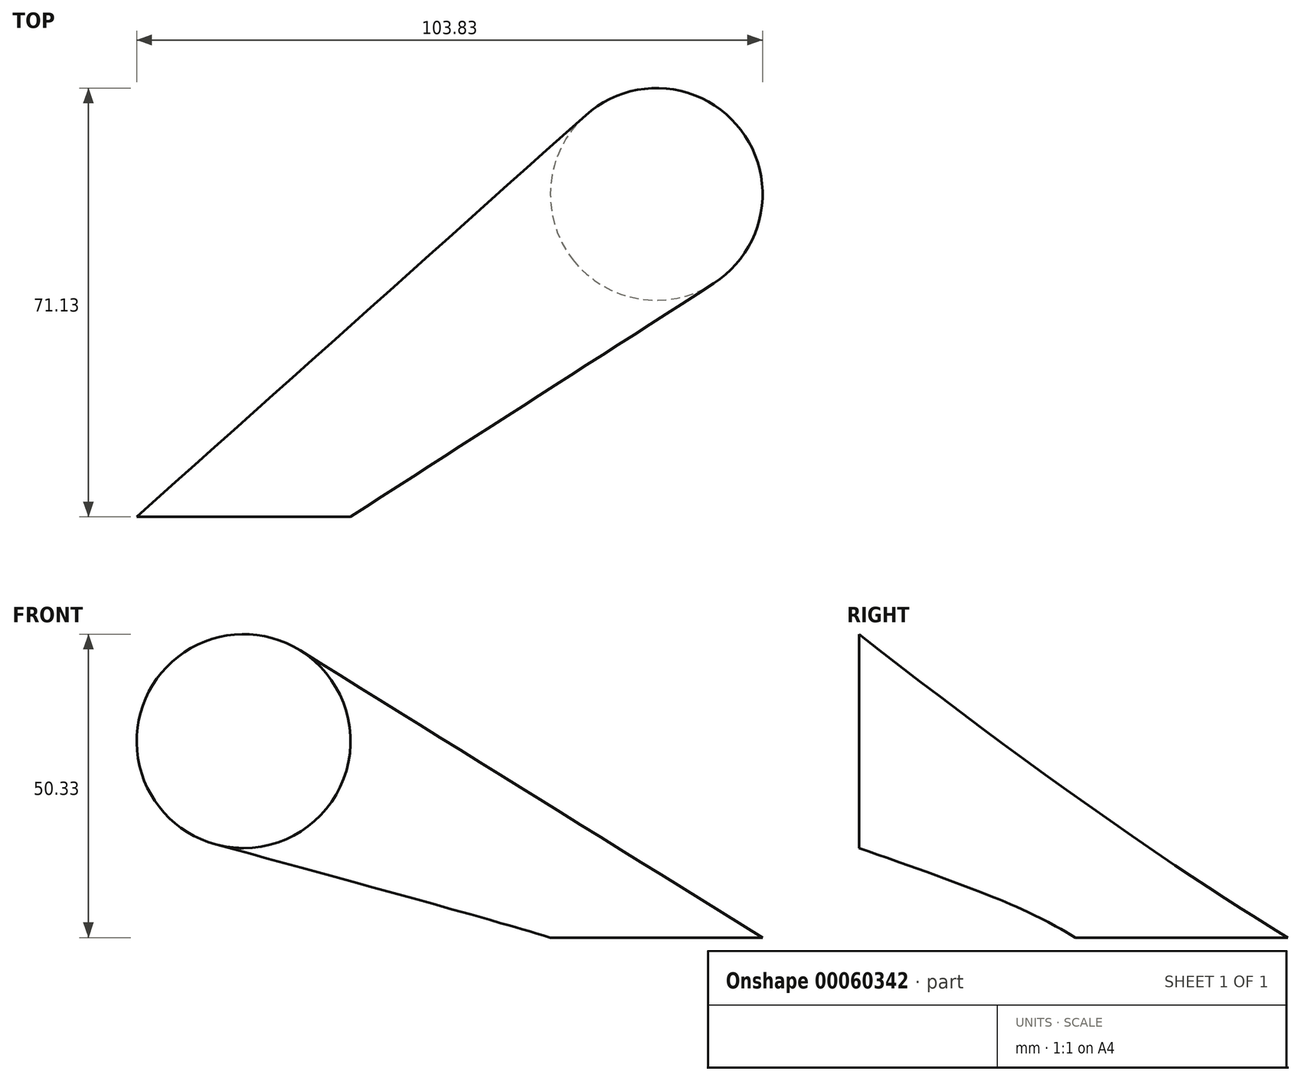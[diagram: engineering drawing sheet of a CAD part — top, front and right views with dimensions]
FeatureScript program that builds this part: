
annotation { "Feature Type Name" : "Feature", "Feature Type Description" : "" }
export const myFeature = defineFeature(function(context is Context, id is Id, definition is map)
    precondition{}
    {
        {
            var Q0;
            Q0=qCreatedBy(makeId("Front.planeOp"),FACE);
            var sketch = newSketch(context, id + "F0", { "sketchPlane" : qUnion([Q0])});
            skCircle(sketch, "E0", {"center": v(-20.34, 32.59) * mm, "radius": 17.74 * mm});
            skSolve(sketch);
        }
        {
            var Q0;
            Q0=qCreatedBy(makeId("Top.planeOp"),FACE);
            var sketch = newSketch(context, id + "F1", { "sketchPlane" : qUnion([Q0])});
            skCircle(sketch, "E1", {"center": v(48.15, 53.52) * mm, "radius": 17.6 * mm});
            skSolve(sketch);
        }
        {
            var Q0;
            Q0=makeQuery(id+"F0.imprint","IMPRINT",FACE,{"disambiguationData":[TD([[makeQuery(id+"F0.imprint","IMPRINT",EDGE,{"derivedFrom":sQuery(id+"F0.wireOp",EDGE,"E0")}),1.0]])]});
            var Q1;
            Q1=makeQuery(id+"F1.imprint","IMPRINT",FACE,{"disambiguationData":[TD([[makeQuery(id+"F1.imprint","IMPRINT",EDGE,{"derivedFrom":sQuery(id+"F1.wireOp",EDGE,"E1")}),1.0]])]});
            loft(context, id + "F2", {"sheetProfilesArray" : [{ "sheetProfileEntities" : qUnion([Q0]) }, { "sheetProfileEntities" : qUnion([Q1]) }]});
        }
    });
